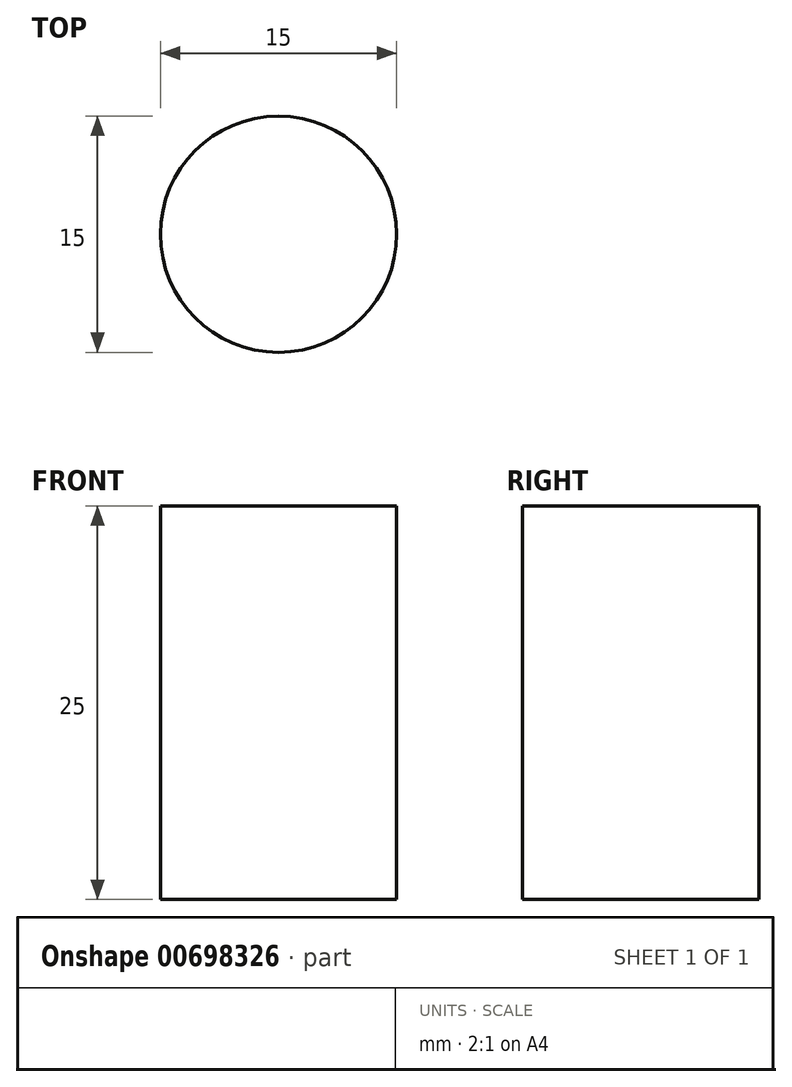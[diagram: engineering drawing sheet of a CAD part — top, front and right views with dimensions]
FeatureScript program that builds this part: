
annotation { "Feature Type Name" : "Feature", "Feature Type Description" : "" }
export const myFeature = defineFeature(function(context is Context, id is Id, definition is map)
    precondition{}
    {
        {
            var Q0;
            Q0=qCreatedBy(makeId("Top.planeOp"),FACE);
            var sketch = newSketch(context, id + "F0", { "sketchPlane" : qUnion([Q0])});
            skCircle(sketch, "E0", {"center": v(0, 0) * mm, "radius": 7.5 * mm});
            skSolve(sketch);
        }
        {
            var Q0;
            Q0 = qSketchRegion(id + "F0", true);
            extrude(context, id + "F1", {"entities" : qUnion([Q0]), "endBound" : BoundingType.SYMMETRIC, "depth" : 25 * mm, "offsetDistance" : 25 * mm});
        }
    });
